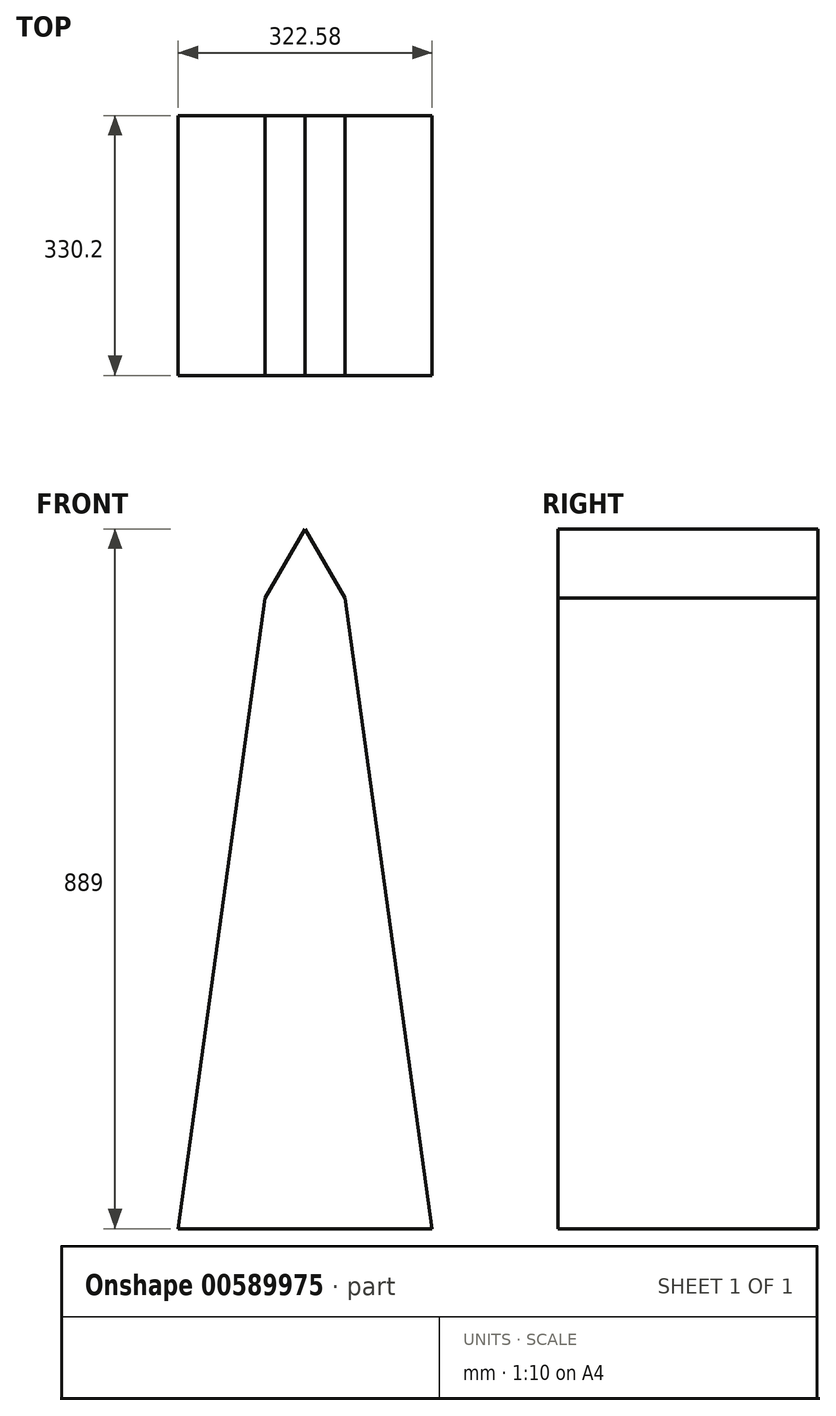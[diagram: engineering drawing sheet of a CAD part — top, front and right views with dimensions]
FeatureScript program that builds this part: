
annotation { "Feature Type Name" : "Feature", "Feature Type Description" : "" }
export const myFeature = defineFeature(function(context is Context, id is Id, definition is map)
    precondition{}
    {
        {
            var Q0;
            Q0=qCreatedBy(makeId("Front.planeOp"),FACE);
            var sketch = newSketch(context, id + "F0", { "sketchPlane" : qUnion([Q0])});
            skLineSegment(sketch, "E0", {"start": v(-161.3, 0) * mm, "end": v(-50.8, 801.01) * mm});
            skLineSegment(sketch, "E1", {"start": v(-50.8, 801.01) * mm, "end": v(0, 889) * mm});
            skLineSegment(sketch, "E2", {"start": v(0, 889) * mm, "end": v(50.8, 801.01) * mm});
            skLineSegment(sketch, "E3", {"start": v(50.8, 801.01) * mm, "end": v(161.3, 0) * mm});
            skLineSegment(sketch, "E4", {"start": v(161.29, 0) * mm, "end": v(-161.3, 0) * mm});
            skLineSegment(sketch, "E5", {"start": v(0, 0) * mm, "end": v(0, -139.35) * mm, "construction": true});
            skSolve(sketch);
        }
        {
            var Q0;
            Q0=makeQuery(id+"F0.imprint","IMPRINT",FACE,{"disambiguationData":[TD([[makeQuery(id+"F0.imprint","IMPRINT",EDGE,{"derivedFrom":sQuery(id+"F0.wireOp",EDGE,"E0")}),-1.0]])]});
            extrude(context, id + "F1", {"entities" : qUnion([Q0]), "depth" : 330.2 * mm, "offsetDistance" : 25.4 * mm});
        }
    });
